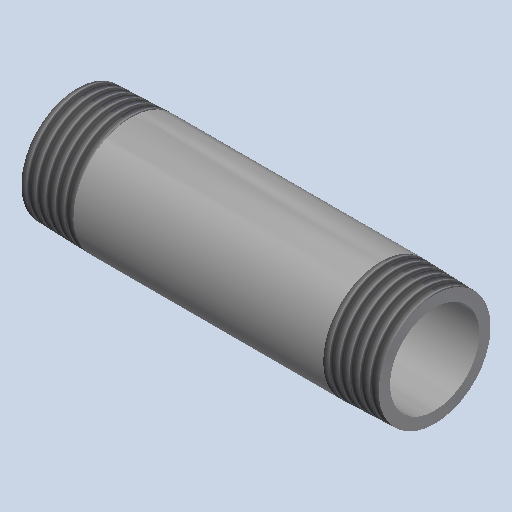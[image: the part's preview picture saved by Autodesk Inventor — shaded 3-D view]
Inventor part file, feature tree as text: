
AUTODESK INVENTOR PART (.ipt)
format: ipt  version: 2025 (Build 290162000, 162)  size: 216,064 bytes
history: native  units: mm (DEFAULTED — no unit token found)
features: other x8, revolve x1
ambient origin geometry x8: Origin, YZ Plane, XZ Plane, XY Plane, X Axis, Y Axis, Z Axis, Center Point
bodies: Solid1 (feature_tree)
feature tree (9):
  revolve  "Revolution1"  [1 undecoded]
  other  "Work Axis1"
  other  "Work Point5"
  other  "Work Axis2"
  other  "Work Point6"
  other  "Work Axis3"
  other  "Work Axis4"
  other  "Work Point7"
  other  "Work Point8"
note: 1 required parameter value undecoded (feature->parameter linkage not recoverable at this tier; creation-order binding heuristic only, values carry confidence <= 0.55)
